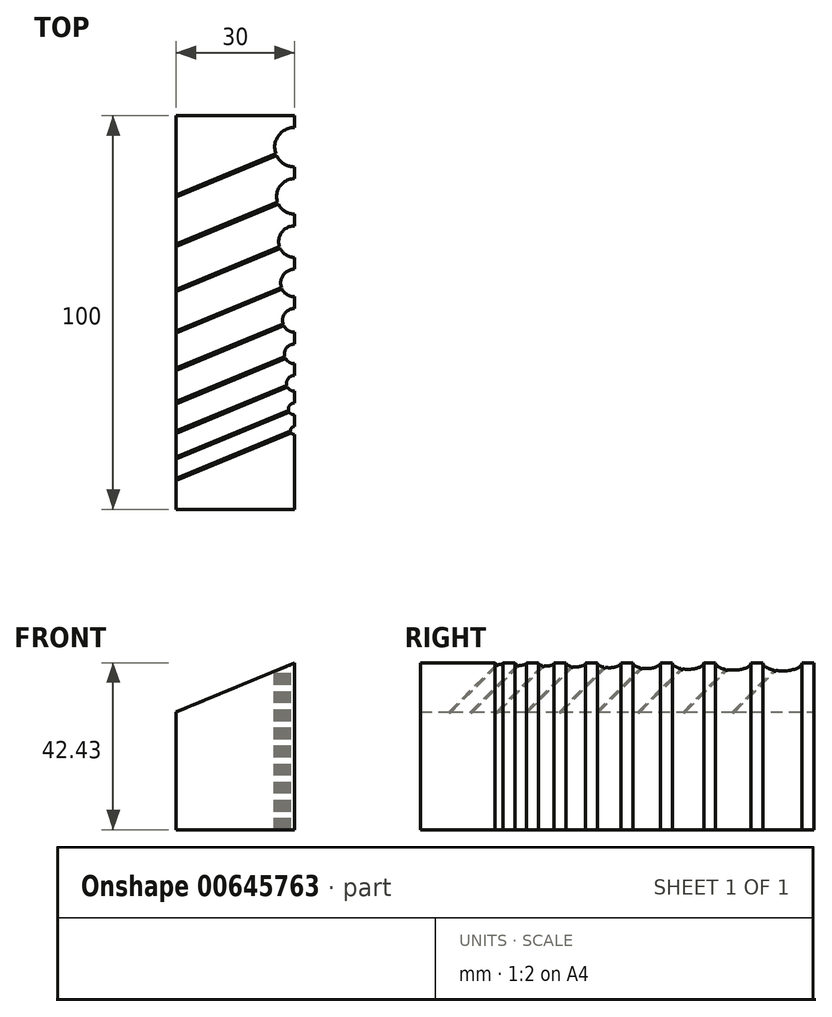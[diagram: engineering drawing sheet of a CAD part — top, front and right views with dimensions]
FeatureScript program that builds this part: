
annotation { "Feature Type Name" : "Feature", "Feature Type Description" : "" }
export const myFeature = defineFeature(function(context is Context, id is Id, definition is map)
    precondition{}
    {
        {
            var Q0;
            Q0=qCreatedBy(makeId("Front.planeOp"),FACE);
            var sketch = newSketch(context, id + "F0", { "sketchPlane" : qUnion([Q0])});
            skLineSegment(sketch, "E0", {"start": v(0, 42.43) * mm, "end": v(-30, 30) * mm});
            skLineSegment(sketch, "E1", {"start": v(-30, 30) * mm, "end": v(-30, 0) * mm});
            skLineSegment(sketch, "E2", {"start": v(-30, 0) * mm, "end": v(0, 0) * mm});
            skLineSegment(sketch, "E3", {"start": v(0, 0) * mm, "end": v(0, 42.43) * mm});
            skSolve(sketch);
        }
        {
            var Q0;
            Q0 = qSketchRegion(id + "F0", true);
            extrude(context, id + "F1", {"entities" : qUnion([Q0]), "depth" : 100 * mm, "offsetDistance" : 25 * mm});
        }
        {
            var Q0;
            Q0=qCreatedBy(makeId("Top.planeOp"),FACE);
            var Q1;
            Q1=makeQuery(id+"F1.opExtrude","CAP_VERTEX",VERTEX,{"disambiguationData":[OSD([sQuery(id+"F0.wireOp",EDGE,"E0"),sQuery(id+"F0.wireOp",EDGE,"E3")])],"isStart":true});
            cPlane(context, id + "F2", {"entities" : qUnion([Q0, Q1]), "cplaneType" : CPlaneType.PLANE_POINT, "offset" : 25 * mm, "width" : 150 * mm, "height" : 150 * mm});
        }
        {
            var Q0;
            Q0=qCreatedBy(id+"F2.planeOp",FACE);
            var sketch = newSketch(context, id + "F3", { "sketchPlane" : qUnion([Q0])});
            skCircle(sketch, "E4", {"center": v(0, -8) * mm, "radius": 5 * mm});
            skCircle(sketch, "E5", {"center": v(0, -20.5) * mm, "radius": 4.5 * mm});
            skCircle(sketch, "E6", {"center": v(0, -32) * mm, "radius": 4 * mm});
            skCircle(sketch, "E7", {"center": v(0, -42.5) * mm, "radius": 3.5 * mm});
            skCircle(sketch, "E8", {"center": v(0, -52) * mm, "radius": 3 * mm});
            skCircle(sketch, "E9", {"center": v(0, -60.5) * mm, "radius": 2.5 * mm});
            skCircle(sketch, "E10", {"center": v(0, -68) * mm, "radius": 2 * mm});
            skCircle(sketch, "E11", {"center": v(0, -74.5) * mm, "radius": 1.5 * mm});
            skCircle(sketch, "E12", {"center": v(0, -80) * mm, "radius": 1 * mm});
            skLineSegment(sketch, "E13.0", {"start": v(-30, -100) * mm, "end": v(-30, 0) * mm, "construction": true});
            skLineSegment(sketch, "E14", {"start": v(0, -8) * mm, "end": v(-30, -20.43) * mm, "construction": true});
            skLineSegment(sketch, "E15", {"start": v(0, -20.5) * mm, "end": v(-30, -32.93) * mm, "construction": true});
            skLineSegment(sketch, "E16", {"start": v(0, -32) * mm, "end": v(-30, -44.43) * mm, "construction": true});
            skLineSegment(sketch, "E17", {"start": v(0, -42.5) * mm, "end": v(-30, -54.93) * mm, "construction": true});
            skLineSegment(sketch, "E18", {"start": v(0, -52) * mm, "end": v(-30, -64.43) * mm, "construction": true});
            skLineSegment(sketch, "E19", {"start": v(0, -60.5) * mm, "end": v(-30, -72.93) * mm, "construction": true});
            skLineSegment(sketch, "E20", {"start": v(0, -68) * mm, "end": v(-30, -80.43) * mm, "construction": true});
            skLineSegment(sketch, "E21", {"start": v(0, -74.5) * mm, "end": v(-30, -86.93) * mm, "construction": true});
            skLineSegment(sketch, "E22", {"start": v(0, -80) * mm, "end": v(-30, -92.43) * mm, "construction": true});
            skSolve(sketch);
        }
        {
            var Q0;
            Q0=qCreatedBy(makeId("Top.planeOp"),FACE);
            var Q1;
            Q1=makeQuery(id+"F1.opExtrude","CAP_VERTEX",VERTEX,{"disambiguationData":[OSD([sQuery(id+"F0.wireOp",EDGE,"E0"),sQuery(id+"F0.wireOp",EDGE,"E1")])],"isStart":false});
            cPlane(context, id + "F4", {"entities" : qUnion([Q0, Q1]), "cplaneType" : CPlaneType.PLANE_POINT, "offset" : 25 * mm, "width" : 150 * mm, "height" : 150 * mm});
        }
        {
            var Q0;
            Q0=qCreatedBy(id+"F4.planeOp",FACE);
            var sketch = newSketch(context, id + "F5", { "sketchPlane" : qUnion([Q0])});
            skLineSegment(sketch, "E23.0", {"start": v(0, -80) * mm, "end": v(-30, -92.43) * mm, "construction": true});
            skLineSegment(sketch, "E24.0", {"start": v(0, -74.5) * mm, "end": v(-30, -86.93) * mm, "construction": true});
            skLineSegment(sketch, "E25.0", {"start": v(0, -68) * mm, "end": v(-30, -80.43) * mm, "construction": true});
            skLineSegment(sketch, "E26.0.0", {"start": v(0, 0) * mm, "end": v(-30, 0) * mm, "construction": true});
            skLineSegment(sketch, "E26.0.1", {"start": v(-30, 0) * mm, "end": v(-30, -100) * mm, "construction": true});
            skLineSegment(sketch, "E26.0.2", {"start": v(-30, -100) * mm, "end": v(0, -100) * mm, "construction": true});
            skLineSegment(sketch, "E26.0.3", {"start": v(0, -100) * mm, "end": v(0, 0) * mm, "construction": true});
            skLineSegment(sketch, "E27.0", {"start": v(0, -60.5) * mm, "end": v(-30, -72.93) * mm, "construction": true});
            skLineSegment(sketch, "E28.0", {"start": v(0, -52) * mm, "end": v(-30, -64.43) * mm, "construction": true});
            skLineSegment(sketch, "E29.0", {"start": v(0, -42.5) * mm, "end": v(-30, -54.93) * mm, "construction": true});
            skLineSegment(sketch, "E30.0", {"start": v(0, -32) * mm, "end": v(-30, -44.43) * mm, "construction": true});
            skLineSegment(sketch, "E31.0", {"start": v(0, -20.5) * mm, "end": v(-30, -32.93) * mm, "construction": true});
            skLineSegment(sketch, "E32.0", {"start": v(0, -8) * mm, "end": v(-30, -20.43) * mm, "construction": true});
            skSolve(sketch);
        }
        {
            var Q0;
            Q0=makeQuery(id+"F1.opExtrude","SWEPT_FACE",FACE,{"disambiguationData":[OSD([sQuery(id+"F0.wireOp",EDGE,"E0")])]});
            var sketch = newSketch(context, id + "F6", { "sketchPlane" : qUnion([Q0])});
            skPoint(sketch, "E33.0", {"position": v(16.24, -8) * mm});
            skPoint(sketch, "E34.0", {"position": v(-16.24, -20.43) * mm});
            skLineSegment(sketch, "E35", {"start": v(-16.24, -20.43) * mm, "end": v(16.24, -8) * mm, "construction": true});
            skSolve(sketch);
        }
        {
            var Q0;
            Q0=sQuery(id+"F6.wireOp",EDGE,"E35");
            var Q1;
            Q1=makeQuery(id+"F1.opExtrude","CAP_VERTEX",VERTEX,{"disambiguationData":[OSD([sQuery(id+"F0.wireOp",EDGE,"E0"),sQuery(id+"F0.wireOp",EDGE,"E3")])],"isStart":true});
            cPlane(context, id + "F7", {"entities" : qUnion([Q0, Q1]), "cplaneType" : CPlaneType.LINE_POINT, "offset" : 25 * mm, "width" : 150 * mm, "height" : 150 * mm});
        }
        {
            var Q0;
            Q0=qCreatedBy(id+"F7.planeOp",FACE);
            var sketch = newSketch(context, id + "F8", { "sketchPlane" : qUnion([Q0])});
            skPoint(sketch, "E36.0", {"position": v(-13.27, 39.2) * mm});
            skPoint(sketch, "E37.0", {"position": v(-24.95, 39.2) * mm});
            skPoint(sketch, "E38.0", {"position": v(-35.69, 39.2) * mm});
            skPoint(sketch, "E39.0", {"position": v(-45.5, 39.2) * mm});
            skPoint(sketch, "E40.0", {"position": v(-54.37, 39.2) * mm});
            skPoint(sketch, "E41.0", {"position": v(-62.3, 39.2) * mm});
            skPoint(sketch, "E42.0", {"position": v(-69.31, 39.2) * mm});
            skPoint(sketch, "E43.0", {"position": v(-75.38, 39.2) * mm});
            skPoint(sketch, "E44.0", {"position": v(-80.52, 39.2) * mm});
            skCircle(sketch, "E45", {"center": v(-13.27, 39.2) * mm, "radius": 0.25 * mm});
            skCircle(sketch, "E46", {"center": v(-24.95, 39.2) * mm, "radius": 0.25 * mm});
            skCircle(sketch, "E47", {"center": v(-35.69, 39.2) * mm, "radius": 0.25 * mm});
            skCircle(sketch, "E48", {"center": v(-45.5, 39.2) * mm, "radius": 0.25 * mm});
            skCircle(sketch, "E49", {"center": v(-54.37, 39.2) * mm, "radius": 0.25 * mm});
            skCircle(sketch, "E50", {"center": v(-62.3, 39.2) * mm, "radius": 0.25 * mm});
            skCircle(sketch, "E51", {"center": v(-69.31, 39.2) * mm, "radius": 0.25 * mm});
            skCircle(sketch, "E52", {"center": v(-75.38, 39.2) * mm, "radius": 0.25 * mm});
            skCircle(sketch, "E53", {"center": v(-80.52, 39.2) * mm, "radius": 0.25 * mm});
            skSolve(sketch);
        }
        {
            var Q0;
            Q0 = qSketchRegion(id + "F8", true);
            extrude(context, id + "F9", {"entities" : qUnion([Q0]), "operationType" : NewBodyOperationType.REMOVE, "endBound" : BoundingType.THROUGH_ALL, "oppositeDirection" : true, "depth" : 25 * mm, "offsetDistance" : 25 * mm});
        }
        {
            var Q0;
            Q0=makeQuery(id+"F3.imprint","IMPRINT",FACE,{"disambiguationData":[TD([[makeQuery(id+"F3.imprint","IMPRINT",EDGE,{"derivedFrom":sQuery(id+"F3.wireOp",EDGE,"E4")}),1.0]])]});
            var Q1;
            Q1=makeQuery(id+"F3.imprint","IMPRINT",FACE,{"disambiguationData":[TD([[makeQuery(id+"F3.imprint","IMPRINT",EDGE,{"derivedFrom":sQuery(id+"F3.wireOp",EDGE,"E5")}),1.0]])]});
            var Q2;
            Q2=makeQuery(id+"F3.imprint","IMPRINT",FACE,{"disambiguationData":[TD([[makeQuery(id+"F3.imprint","IMPRINT",EDGE,{"derivedFrom":sQuery(id+"F3.wireOp",EDGE,"E6")}),1.0]])]});
            var Q3;
            Q3=makeQuery(id+"F3.imprint","IMPRINT",FACE,{"disambiguationData":[TD([[makeQuery(id+"F3.imprint","IMPRINT",EDGE,{"derivedFrom":sQuery(id+"F3.wireOp",EDGE,"E7")}),1.0]])]});
            var Q4;
            Q4=makeQuery(id+"F3.imprint","IMPRINT",FACE,{"disambiguationData":[TD([[makeQuery(id+"F3.imprint","IMPRINT",EDGE,{"derivedFrom":sQuery(id+"F3.wireOp",EDGE,"E8")}),1.0]])]});
            var Q5;
            Q5=makeQuery(id+"F3.imprint","IMPRINT",FACE,{"disambiguationData":[TD([[makeQuery(id+"F3.imprint","IMPRINT",EDGE,{"derivedFrom":sQuery(id+"F3.wireOp",EDGE,"E9")}),1.0]])]});
            var Q6;
            Q6=makeQuery(id+"F3.imprint","IMPRINT",FACE,{"disambiguationData":[TD([[makeQuery(id+"F3.imprint","IMPRINT",EDGE,{"derivedFrom":sQuery(id+"F3.wireOp",EDGE,"E10")}),1.0]])]});
            var Q7;
            Q7=makeQuery(id+"F3.imprint","IMPRINT",FACE,{"disambiguationData":[TD([[makeQuery(id+"F3.imprint","IMPRINT",EDGE,{"derivedFrom":sQuery(id+"F3.wireOp",EDGE,"E11")}),1.0]])]});
            var Q8;
            Q8=makeQuery(id+"F3.imprint","IMPRINT",FACE,{"disambiguationData":[TD([[makeQuery(id+"F3.imprint","IMPRINT",EDGE,{"derivedFrom":sQuery(id+"F3.wireOp",EDGE,"E12")}),1.0]])]});
            extrude(context, id + "F10", {"entities" : qUnion([Q0, Q1, Q2, Q3, Q4, Q5, Q6, Q7, Q8]), "operationType" : NewBodyOperationType.REMOVE, "endBound" : BoundingType.THROUGH_ALL, "oppositeDirection" : true, "depth" : 25 * mm, "offsetDistance" : 25 * mm});
        }
    });
